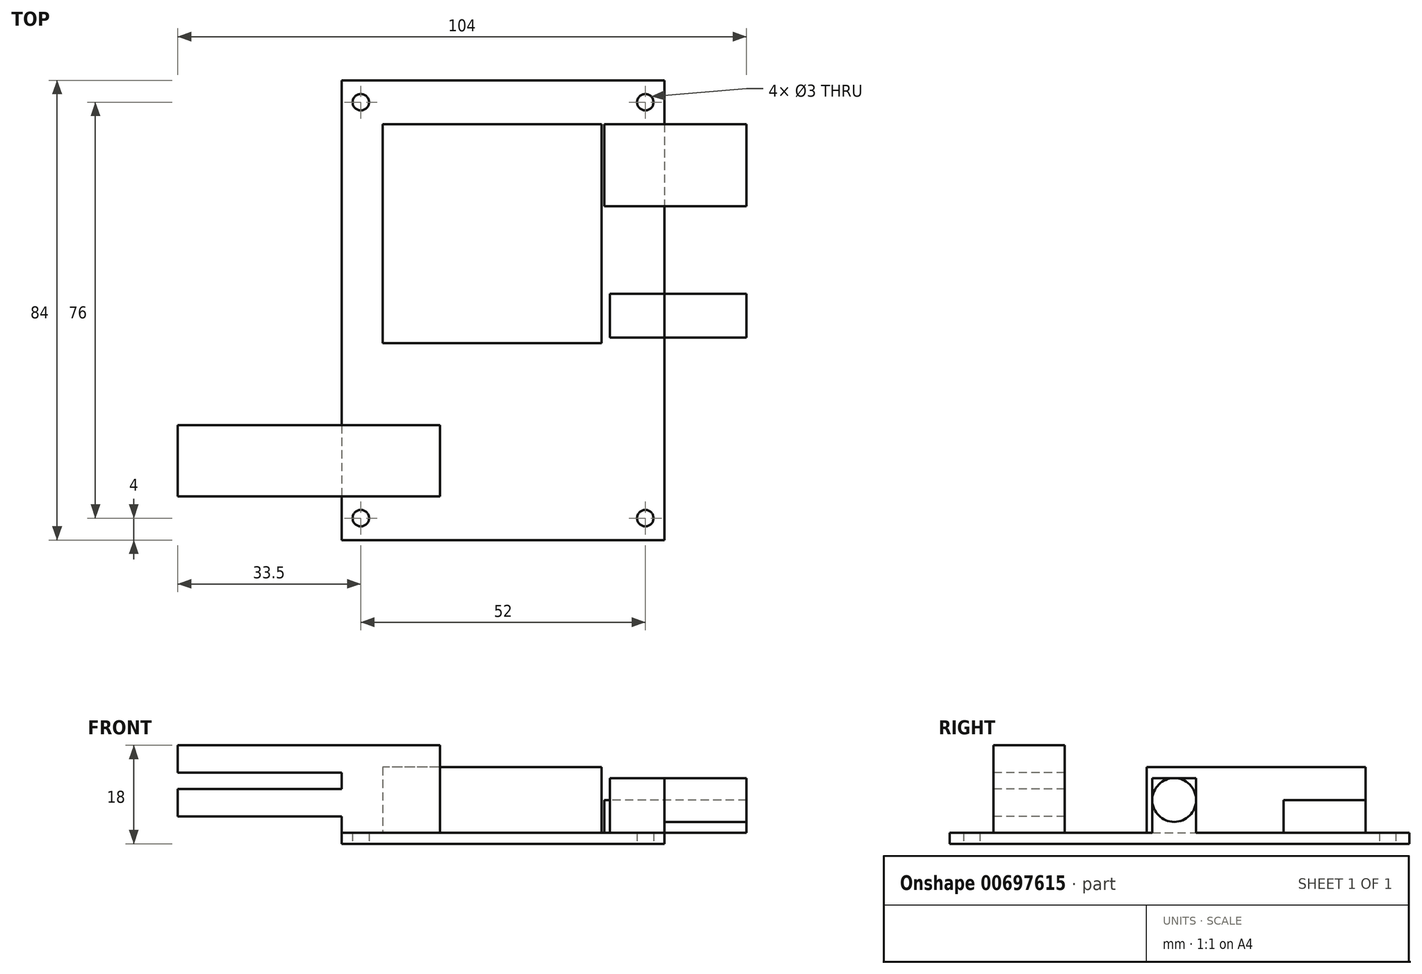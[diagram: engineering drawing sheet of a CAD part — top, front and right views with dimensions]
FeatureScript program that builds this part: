
annotation { "Feature Type Name" : "Feature", "Feature Type Description" : "" }
export const myFeature = defineFeature(function(context is Context, id is Id, definition is map)
    precondition{}
    {
        {
            var Q0;
            Q0=qCreatedBy(makeId("Top.planeOp"),FACE);
            var sketch = newSketch(context, id + "F0", { "sketchPlane" : qUnion([Q0])});
            skLineSegment(sketch, "E0.bottom", {"start": v(29.5, -42) * mm, "end": v(-29.5, -42) * mm});
            skLineSegment(sketch, "E0.top", {"start": v(29.5, 42) * mm, "end": v(-29.5, 42) * mm});
            skLineSegment(sketch, "E0.left", {"start": v(29.5, -42) * mm, "end": v(29.5, 42) * mm});
            skLineSegment(sketch, "E0.right", {"start": v(-29.5, -42) * mm, "end": v(-29.5, 42) * mm});
            skPoint(sketch, "E0.middle", {"position": v(0, 0) * mm});
            skCircle(sketch, "E1", {"center": v(-26, 38) * mm, "radius": 1.5 * mm});
            skCircle(sketch, "E2.MirrorC", {"center": v(26, 38) * mm, "radius": 1.5 * mm});
            skCircle(sketch, "E3.MirrorC", {"center": v(-26, -38) * mm, "radius": 1.5 * mm});
            skCircle(sketch, "E4.MirrorC", {"center": v(26, -38) * mm, "radius": 1.5 * mm});
            skSolve(sketch);
        }
        {
            var Q0;
            Q0 = qSketchRegion(id + "F0", true);
            extrude(context, id + "F1", {"entities" : qUnion([Q0]), "depth" : 2 * mm, "offsetDistance" : 25 * mm});
        }
        {
            var Q0;
            Q0=makeQuery(id+"F1.opExtrude","CAP_FACE",FACE,{"disambiguationData":[OSD([sQuery(id+"F0.wireOp",EDGE,"E0.bottom"),sQuery(id+"F0.wireOp",EDGE,"E0.top"),sQuery(id+"F0.wireOp",EDGE,"E0.left"),sQuery(id+"F0.wireOp",EDGE,"E0.right"),sQuery(id+"F0.wireOp",EDGE,"E1"),sQuery(id+"F0.wireOp",EDGE,"E2.MirrorC"),sQuery(id+"F0.wireOp",EDGE,"E3.MirrorC"),sQuery(id+"F0.wireOp",EDGE,"E4.MirrorC")])],"isStart":false});
            var sketch = newSketch(context, id + "F2", { "sketchPlane" : qUnion([Q0])});
            skLineSegment(sketch, "E5.bottom", {"start": v(18, -6) * mm, "end": v(-22, -6) * mm});
            skLineSegment(sketch, "E5.top", {"start": v(18, 34) * mm, "end": v(-22, 34) * mm});
            skLineSegment(sketch, "E5.left", {"start": v(18, -6) * mm, "end": v(18, 34) * mm});
            skLineSegment(sketch, "E5.right", {"start": v(-22, -6) * mm, "end": v(-22, 34) * mm});
            skPoint(sketch, "E5.middle", {"position": v(-2, 14) * mm});
            skSolve(sketch);
        }
        {
            var Q0;
            Q0=makeQuery(id+"F2.imprint","IMPRINT",FACE,{"disambiguationData":[TD([[makeQuery(id+"F2.imprint","IMPRINT",EDGE,{"derivedFrom":sQuery(id+"F2.wireOp",EDGE,"E5.bottom")}),-1.0]])]});
            extrude(context, id + "F3", {"entities" : qUnion([Q0]), "operationType" : NewBodyOperationType.ADD, "depth" : 12 * mm, "offsetDistance" : 25 * mm});
        }
        {
            var Q0;
            Q0=makeQuery(id+"F1.opExtrude","CAP_FACE",FACE,{"disambiguationData":[OSD([sQuery(id+"F0.wireOp",EDGE,"E0.bottom"),sQuery(id+"F0.wireOp",EDGE,"E0.top"),sQuery(id+"F0.wireOp",EDGE,"E0.left"),sQuery(id+"F0.wireOp",EDGE,"E0.right"),sQuery(id+"F0.wireOp",EDGE,"E1"),sQuery(id+"F0.wireOp",EDGE,"E2.MirrorC"),sQuery(id+"F0.wireOp",EDGE,"E3.MirrorC"),sQuery(id+"F0.wireOp",EDGE,"E4.MirrorC")])],"isStart":false});
            var sketch = newSketch(context, id + "F4", { "sketchPlane" : qUnion([Q0])});
            skLineSegment(sketch, "E6.bottom", {"start": v(-29.5, -21) * mm, "end": v(-11.5, -21) * mm});
            skLineSegment(sketch, "E6.top", {"start": v(-29.5, -34) * mm, "end": v(-11.5, -34) * mm});
            skLineSegment(sketch, "E6.left", {"start": v(-29.5, -21) * mm, "end": v(-29.5, -34) * mm});
            skLineSegment(sketch, "E6.right", {"start": v(-11.5, -21) * mm, "end": v(-11.5, -34) * mm});
            skSolve(sketch);
        }
        {
            var Q0;
            Q0 = qSketchRegion(id + "F4", true);
            extrude(context, id + "F5", {"entities" : qUnion([Q0]), "operationType" : NewBodyOperationType.ADD, "depth" : 16 * mm, "offsetDistance" : 25 * mm});
        }
        {
            var Q0;
            Q0=makeQuery(id+"F5.boolean.opBoolean","MERGE",FACE,{"derivedFrom":[makeQuery(id+"F1.opExtrude","SWEPT_FACE",FACE,{"disambiguationData":[OSD([sQuery(id+"F0.wireOp",EDGE,"E0.right")])]}),makeQuery(id+"F5.opExtrude","SWEPT_FACE",FACE,{"disambiguationData":[OSD([sQuery(id+"F4.wireOp",EDGE,"E6.left")])]})]});
            var sketch = newSketch(context, id + "F6", { "sketchPlane" : qUnion([Q0])});
            skLineSegment(sketch, "E7.bottom", {"start": v(21, 18) * mm, "end": v(34, 18) * mm});
            skLineSegment(sketch, "E7.top", {"start": v(21, 13) * mm, "end": v(34, 13) * mm});
            skLineSegment(sketch, "E7.left", {"start": v(21, 18) * mm, "end": v(21, 13) * mm});
            skLineSegment(sketch, "E7.right", {"start": v(34, 18) * mm, "end": v(34, 13) * mm});
            skLineSegment(sketch, "E8.bottom", {"start": v(21, 5) * mm, "end": v(34, 5) * mm});
            skLineSegment(sketch, "E8.top", {"start": v(21, 10) * mm, "end": v(34, 10) * mm});
            skLineSegment(sketch, "E8.left", {"start": v(21, 5) * mm, "end": v(21, 10) * mm});
            skLineSegment(sketch, "E8.right", {"start": v(34, 5) * mm, "end": v(34, 10) * mm});
            skSolve(sketch);
        }
        {
            var Q0;
            Q0=makeQuery(id+"F6.imprint","IMPRINT",FACE,{"disambiguationData":[TD([[makeQuery(id+"F6.imprint","IMPRINT",EDGE,{"derivedFrom":sQuery(id+"F6.wireOp",EDGE,"E7.bottom")}),1.0]])]});
            var Q1;
            Q1=makeQuery(id+"F6.imprint","IMPRINT",FACE,{"disambiguationData":[TD([[makeQuery(id+"F6.imprint","IMPRINT",EDGE,{"derivedFrom":sQuery(id+"F6.wireOp",EDGE,"E8.bottom")}),1.0]])]});
            extrude(context, id + "F7", {"entities" : qUnion([Q0, Q1]), "operationType" : NewBodyOperationType.ADD, "depth" : 30 * mm, "offsetDistance" : 25 * mm});
        }
        {
            var Q0;
            Q0=makeQuery(id+"F1.opExtrude","CAP_FACE",FACE,{"disambiguationData":[OSD([sQuery(id+"F0.wireOp",EDGE,"E0.bottom"),sQuery(id+"F0.wireOp",EDGE,"E0.top"),sQuery(id+"F0.wireOp",EDGE,"E0.left"),sQuery(id+"F0.wireOp",EDGE,"E0.right"),sQuery(id+"F0.wireOp",EDGE,"E1"),sQuery(id+"F0.wireOp",EDGE,"E2.MirrorC"),sQuery(id+"F0.wireOp",EDGE,"E3.MirrorC"),sQuery(id+"F0.wireOp",EDGE,"E4.MirrorC")])],"isStart":false});
            var sketch = newSketch(context, id + "F8", { "sketchPlane" : qUnion([Q0])});
            skLineSegment(sketch, "E9.bottom", {"start": v(29.5, 3) * mm, "end": v(19.5, 3) * mm});
            skLineSegment(sketch, "E9.top", {"start": v(29.5, -5) * mm, "end": v(19.5, -5) * mm});
            skLineSegment(sketch, "E9.left", {"start": v(29.5, 3) * mm, "end": v(29.5, -5) * mm});
            skLineSegment(sketch, "E9.right", {"start": v(19.5, 3) * mm, "end": v(19.5, -5) * mm});
            skSolve(sketch);
        }
        {
            var Q0;
            Q0 = qSketchRegion(id + "F8", true);
            extrude(context, id + "F9", {"entities" : qUnion([Q0]), "operationType" : NewBodyOperationType.ADD, "depth" : 10 * mm, "offsetDistance" : 25 * mm});
        }
        {
            var Q0;
            Q0=makeQuery(id+"F9.boolean.opBoolean","MERGE",FACE,{"derivedFrom":[makeQuery(id+"F1.opExtrude","SWEPT_FACE",FACE,{"disambiguationData":[OSD([sQuery(id+"F0.wireOp",EDGE,"E0.left")])]}),makeQuery(id+"F9.opExtrude","SWEPT_FACE",FACE,{"disambiguationData":[OSD([sQuery(id+"F8.wireOp",EDGE,"E9.left")])]})]});
            var sketch = newSketch(context, id + "F10", { "sketchPlane" : qUnion([Q0])});
            skCircle(sketch, "E10", {"center": v(-1, 8) * mm, "radius": 4 * mm});
            skSolve(sketch);
        }
        {
            var Q0;
            Q0 = qSketchRegion(id + "F10", true);
            extrude(context, id + "F11", {"entities" : qUnion([Q0]), "operationType" : NewBodyOperationType.ADD, "depth" : 15 * mm, "offsetDistance" : 25 * mm});
        }
        {
            var Q0;
            Q0=makeQuery(id+"F1.opExtrude","CAP_FACE",FACE,{"disambiguationData":[OSD([sQuery(id+"F0.wireOp",EDGE,"E0.bottom"),sQuery(id+"F0.wireOp",EDGE,"E0.top"),sQuery(id+"F0.wireOp",EDGE,"E0.left"),sQuery(id+"F0.wireOp",EDGE,"E0.right"),sQuery(id+"F0.wireOp",EDGE,"E1"),sQuery(id+"F0.wireOp",EDGE,"E2.MirrorC"),sQuery(id+"F0.wireOp",EDGE,"E3.MirrorC"),sQuery(id+"F0.wireOp",EDGE,"E4.MirrorC")])],"isStart":false});
            var sketch = newSketch(context, id + "F12", { "sketchPlane" : qUnion([Q0])});
            skLineSegment(sketch, "E11.bottom", {"start": v(29.5, 34) * mm, "end": v(18.5, 34) * mm});
            skLineSegment(sketch, "E11.top", {"start": v(29.5, 19) * mm, "end": v(18.5, 19) * mm});
            skLineSegment(sketch, "E11.left", {"start": v(29.5, 34) * mm, "end": v(29.5, 19) * mm});
            skLineSegment(sketch, "E11.right", {"start": v(18.5, 34) * mm, "end": v(18.5, 19) * mm});
            skSolve(sketch);
        }
        {
            var Q0;
            Q0 = qSketchRegion(id + "F12", true);
            extrude(context, id + "F13", {"entities" : qUnion([Q0]), "operationType" : NewBodyOperationType.ADD, "depth" : 6 * mm, "offsetDistance" : 25 * mm});
        }
        {
            var Q0;
            {var subQ0=sQuery(id+"F0.wireOp",EDGE,"E0.top");var subQ1=sQuery(id+"F0.wireOp",EDGE,"E4.MirrorC");var subQ2=sQuery(id+"F0.wireOp",EDGE,"E3.MirrorC");var subQ3=sQuery(id+"F0.wireOp",EDGE,"E2.MirrorC");var subQ4=sQuery(id+"F0.wireOp",EDGE,"E1");var subQ5=sQuery(id+"F0.wireOp",EDGE,"E0.right");var subQ6=sQuery(id+"F0.wireOp",EDGE,"E0.left");var subQ7=sQuery(id+"F0.wireOp",EDGE,"E0.bottom");var subQ8=makeQuery(id+"F1.opExtrude","SWEPT_FACE",FACE,{"disambiguationData":[OSD([subQ6])]});var subQ9=makeQuery(id+"F9.opExtrude","SWEPT_FACE",FACE,{"disambiguationData":[OSD([sQuery(id+"F8.wireOp",EDGE,"E9.left")])]});Q0=makeQuery(id+"F13.boolean.opBoolean","MERGE",FACE,{"derivedFrom":[makeQuery(id+"F11.boolean.opBoolean","SPLIT",FACE,{"disambiguationData":[TD([makeQuery(id+"F1.opExtrude","SWEPT_FACE",FACE,{"disambiguationData":[OSD([subQ7])]}),makeQuery(id+"F1.opExtrude","CAP_FACE",FACE,{"disambiguationData":[OSD([subQ7,subQ0,subQ6,subQ5,subQ4,subQ3,subQ2,subQ1])],"isStart":true}),makeQuery(id+"F1.opExtrude","CAP_FACE",FACE,{"disambiguationData":[OSD([subQ7,subQ0,subQ6,subQ5,subQ4,subQ3,subQ2,subQ1])],"isStart":false}),makeQuery(id+"F1.opExtrude","SWEPT_FACE",FACE,{"disambiguationData":[OSD([subQ0])]}),subQ8,makeQuery(id+"F9.opExtrude","SWEPT_FACE",FACE,{"disambiguationData":[OSD([sQuery(id+"F8.wireOp",EDGE,"E9.bottom")])]}),makeQuery(id+"F9.opExtrude","SWEPT_FACE",FACE,{"disambiguationData":[OSD([sQuery(id+"F8.wireOp",EDGE,"E9.top")])]}),subQ9,makeQuery(id+"F11.opExtrude","SWEPT_FACE",FACE,{"disambiguationData":[OSD([sQuery(id+"F10.wireOp",EDGE,"E10")])]})])],"derivedFrom":makeQuery(id+"F9.boolean.opBoolean","MERGE",FACE,{"derivedFrom":[subQ8,subQ9]})}),makeQuery(id+"F13.opExtrude","SWEPT_FACE",FACE,{"disambiguationData":[OSD([sQuery(id+"F12.wireOp",EDGE,"E11.left")])]})]});}
            var sketch = newSketch(context, id + "F14", { "sketchPlane" : qUnion([Q0])});
            skLineSegment(sketch, "E12.bottom", {"start": v(34, 8) * mm, "end": v(19, 8) * mm});
            skLineSegment(sketch, "E12.top", {"start": v(34, 2) * mm, "end": v(19, 2) * mm});
            skLineSegment(sketch, "E12.left", {"start": v(34, 8) * mm, "end": v(34, 2) * mm});
            skLineSegment(sketch, "E12.right", {"start": v(19, 8) * mm, "end": v(19, 2) * mm});
            skSolve(sketch);
        }
        {
            var Q0;
            Q0 = qSketchRegion(id + "F14", true);
            extrude(context, id + "F15", {"entities" : qUnion([Q0]), "operationType" : NewBodyOperationType.ADD, "depth" : 15 * mm, "offsetDistance" : 25 * mm});
        }
    });
